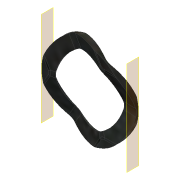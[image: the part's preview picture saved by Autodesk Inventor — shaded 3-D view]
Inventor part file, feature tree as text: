
AUTODESK INVENTOR PART (.ipt)
format: ipt  version: 2020.2 (Build 242310000, 310)  size: 236,032 bytes
history: native  units: mm
features: extrude x3, sketch x3, plane x2, mirror x2, pattern_circular x2, fillet x1
ambient origin geometry x8: Origin, YZ Plane, XZ Plane, XY Plane, X Axis, Y Axis, Z Axis, Center Point
bodies: Body1 (feature_tree)
feature tree (13):
  extrude  "Extrusion7"  Depth=15.5mm
  plane  "Work Plane6"
  extrude  "Extrusion10"  Depth=2.0mm
  mirror  "Mirror5"
  pattern_circular  "Circular Pattern2"  [2 undecoded]
  plane  "Work Plane7"
  extrude  "Extrusion11"  Depth=7.75mm TaperAngle=0.0deg
  mirror  "Mirror6"
  pattern_circular  "Circular Pattern3"  Count=3 Angle=360.0deg
  fillet  "Fillet8"  Radius=1.0mm
  sketch  "Sketch11"  dims[d82=11.0mm d83=15.5mm]
  sketch  "Sketch14"  dims[d84=2.0mm d85=0.0mm d100=2.0mm]
  sketch  "Sketch15"  dims[d101=0.3mm d102=1.0mm d104=7.75mm d105=0.0mm d106=30.0mm d107=360.0deg d109=1.0mm d110=2.0mm d111=0.3mm d112=7.75mm d113=0.0mm d114=30.0mm d115=360.0deg d117=3.0mm]
note: 2 required parameter values undecoded (feature->parameter linkage not recoverable at this tier; creation-order binding heuristic only, values carry confidence <= 0.55)
